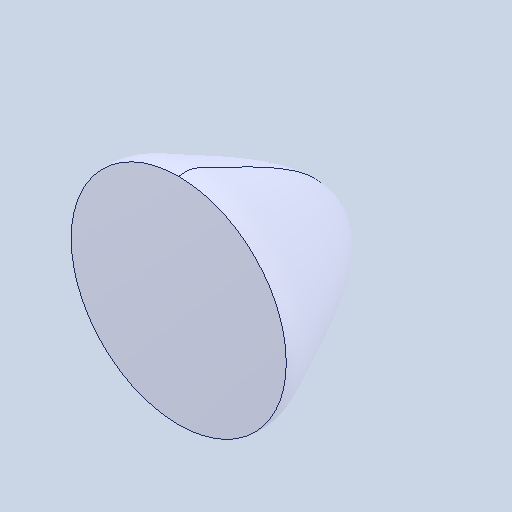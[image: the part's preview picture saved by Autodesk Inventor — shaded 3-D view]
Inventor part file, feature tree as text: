
AUTODESK INVENTOR PART (.ipt)
format: ipt  version: 2024 (Build 280153000, 153)  size: 155,648 bytes
history: native  units: in
note: dims shown in document units (in); Inventor stores cm internally (conversion verified against a paired STEP export)
features: revolve x1
ambient origin geometry x8: Origin, YZ Plane, XZ Plane, XY Plane, X Axis, Y Axis, Z Axis, Center Point
bodies: Solid1 (feature_tree)
feature tree (1):
  revolve  "Revolve1"  [1 undecoded]
note: 1 required parameter value undecoded (feature->parameter linkage not recoverable at this tier; creation-order binding heuristic only, values carry confidence <= 0.55)
